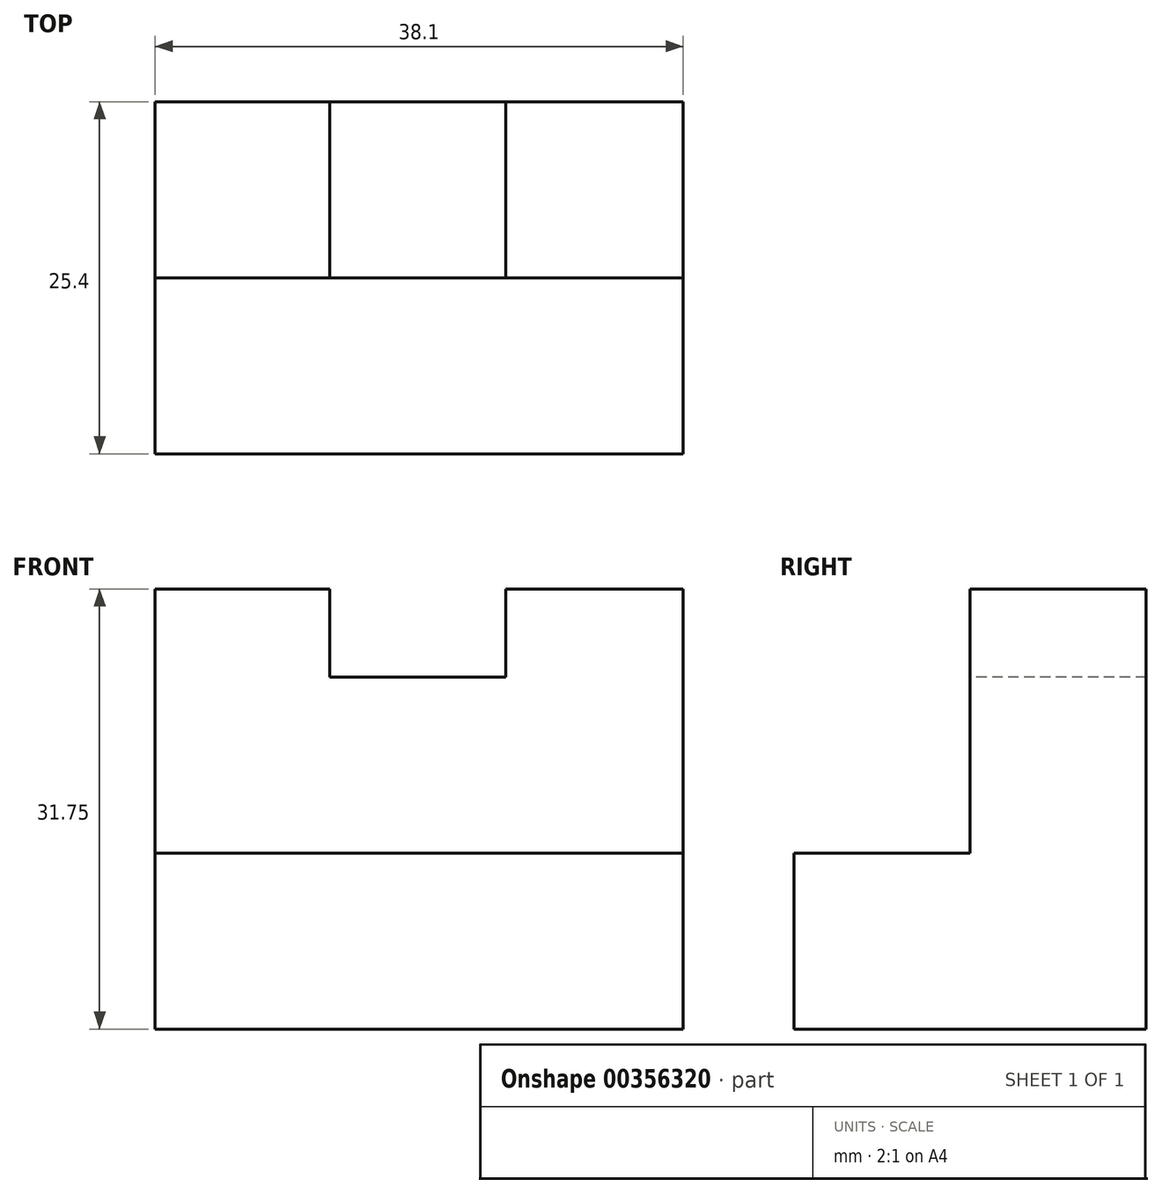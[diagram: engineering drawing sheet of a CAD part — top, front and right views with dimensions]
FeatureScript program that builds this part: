
annotation { "Feature Type Name" : "Feature", "Feature Type Description" : "" }
export const myFeature = defineFeature(function(context is Context, id is Id, definition is map)
    precondition{}
    {
        {
            var Q0;
            Q0=qCreatedBy(makeId("Right.planeOp"),FACE);
            var sketch = newSketch(context, id + "F0", { "sketchPlane" : qUnion([Q0])});
            skLineSegment(sketch, "E0", {"start": v(12.7, 31.75) * mm, "end": v(25.4, 31.75) * mm});
            skLineSegment(sketch, "E1", {"start": v(25.4, 31.75) * mm, "end": v(25.4, 0) * mm});
            skLineSegment(sketch, "E2", {"start": v(25.4, 0) * mm, "end": v(0, 0) * mm});
            skLineSegment(sketch, "E3", {"start": v(0, 0) * mm, "end": v(0, 12.7) * mm});
            skLineSegment(sketch, "E4", {"start": v(0, 12.7) * mm, "end": v(12.7, 12.7) * mm});
            skLineSegment(sketch, "E5", {"start": v(12.7, 12.7) * mm, "end": v(12.7, 31.75) * mm});
            skPoint(sketch, "E5.endSnap0", {"position": v(12.7, 31.75) * mm});
            skPoint(sketch, "E6.orphan", {"position": v(0, 31.75) * mm});
            skSolve(sketch);
        }
        {
            var Q0;
            Q0 = qSketchRegion(id + "F0", true);
            extrude(context, id + "F1", {"entities" : qUnion([Q0]), "oppositeDirection" : true, "depth" : 38.1 * mm});
        }
        {
            var Q0;
            Q0=makeQuery(id+"F1.opExtrude","SWEPT_FACE",FACE,{"disambiguationData":[OSD([sQuery(id+"F0.wireOp",EDGE,"E0")])]});
            var sketch = newSketch(context, id + "F2", { "sketchPlane" : qUnion([Q0])});
            skLineSegment(sketch, "E7", {"start": v(-25.5, 25.4) * mm, "end": v(-25.5, 12.7) * mm});
            skLineSegment(sketch, "E8", {"start": v(-25.5, 12.7) * mm, "end": v(-12.8, 12.7) * mm});
            skLineSegment(sketch, "E9", {"start": v(-12.8, 12.7) * mm, "end": v(-12.8, 25.4) * mm});
            skLineSegment(sketch, "E10", {"start": v(-12.8, 25.4) * mm, "end": v(-25.5, 25.4) * mm});
            skSolve(sketch);
        }
        {
            var Q0;
            Q0 = qSketchRegion(id + "F2", true);
            extrude(context, id + "F3", {"entities" : qUnion([Q0]), "operationType" : NewBodyOperationType.REMOVE, "oppositeDirection" : true, "depth" : 6.35 * mm});
        }
    });
